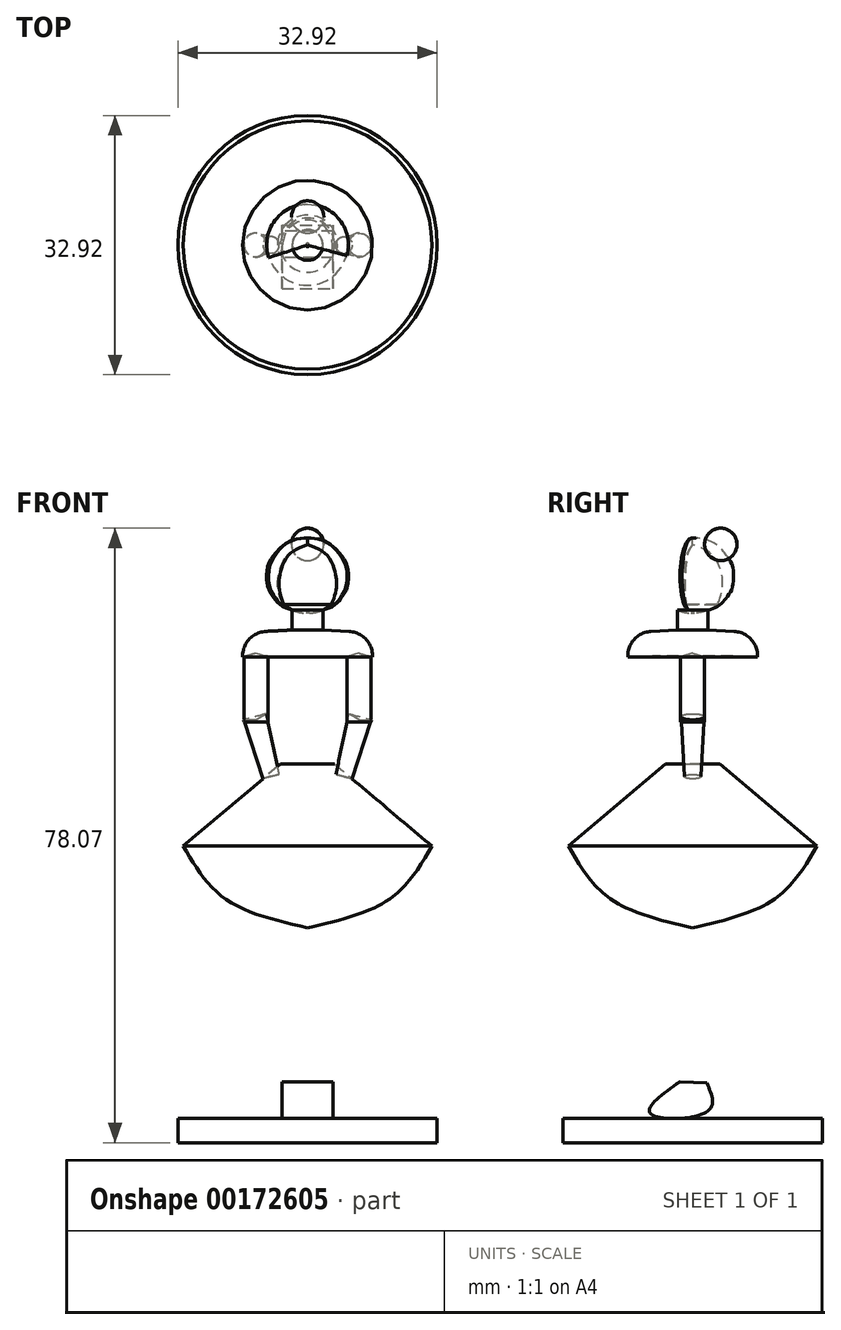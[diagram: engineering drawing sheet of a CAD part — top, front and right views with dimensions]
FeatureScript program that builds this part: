
annotation { "Feature Type Name" : "Feature", "Feature Type Description" : "" }
export const myFeature = defineFeature(function(context is Context, id is Id, definition is map)
    precondition{}
    {
        {
            var Q0;
            Q0=qCreatedBy(makeId("Front.planeOp"),FACE);
            var sketch = newSketch(context, id + "F0", { "sketchPlane" : qUnion([Q0])});
            skFitSpline(sketch, "E0", {"points": [v(-5.4, 24.75) * mm, v(-2.64, 17.55) * mm, v(-3.57, 10.2) * mm], "startDerivative": vector(6.92, -12.61) * mm, "endDerivative": vector(-2.97, -14.09) * mm});
            skLineSegment(sketch, "E1", {"start": v(0, 29.58) * mm, "end": v(0, 9.96) * mm});
            skFitSpline(sketch, "E2", {"points": [v(-3.57, 10.2) * mm, v(0, 9.96) * mm], "startDerivative": vector(3.3, 0.5) * mm, "endDerivative": vector(2.93, 1.66) * mm});
            skLineSegment(sketch, "E3", {"start": v(-5.4, 24.75) * mm, "end": v(0, 24.75) * mm});
            skPoint(sketch, "E3.endSnap0", {"position": v(0, 19.77) * mm});
            skSolve(sketch);
        }
        {
            var Q0;
            Q0 = qSketchRegion(id + "F0", true);
            var Q1;
            Q1=sQuery(id+"F0.wireOp",EDGE,"E0");
            var Q2;
            Q2=sQuery(id+"F0.wireOp",EDGE,"E2");
            var Q3;
            Q3=sQuery(id+"F0.wireOp",EDGE,"E1");
            revolve(context, id + "F1", {"bodyType" : ToolBodyType.SURFACE, "entities" : qUnion([Q0]), "surfaceEntities" : qUnion([Q1, Q2]), "axis" : qUnion([Q3]), "revolveType" : RevolveType.FULL});
        }
        {
            var Q0;
            Q0=qCreatedBy(makeId("Front.planeOp"),FACE);
            var sketch = newSketch(context, id + "F2", { "sketchPlane" : qUnion([Q0])});
            skArc(sketch, "E4", {"start": v(-5.27, 27.27) * mm, "mid": v(-7.42, 26.26) * mm, "end": v(-8.24, 24.04) * mm});
            skLineSegment(sketch, "E5", {"start": v(-8.24, 24.04) * mm, "end": v(-5.1, 24.14) * mm});
            skLineSegment(sketch, "E6", {"start": v(-5.27, 27.27) * mm, "end": v(0, 27.55) * mm});
            skLineSegment(sketch, "E7", {"start": v(-5.1, 24.14) * mm, "end": v(0, 24.14) * mm});
            skLineSegment(sketch, "E8", {"start": v(0, 24.14) * mm, "end": v(0, 27.55) * mm});
            skSolve(sketch);
        }
        {
            var Q0;
            Q0=makeQuery(id+"F2.imprint","IMPRINT",FACE,{"disambiguationData":[TD([[makeQuery(id+"F2.imprint","IMPRINT",EDGE,{"derivedFrom":sQuery(id+"F2.wireOp",EDGE,"E4")}),1.0]])]});
            var Q1;
            Q1=sQuery(id+"F2.wireOp",EDGE,"E8");
            revolve(context, id + "F3", {"entities" : qUnion([Q0]), "axis" : qUnion([Q1]), "revolveType" : RevolveType.FULL});
        }
        {
            var Q0;
            Q0=qCreatedBy(makeId("Front.planeOp"),FACE);
            var sketch = newSketch(context, id + "F4", { "sketchPlane" : qUnion([Q0])});
            skLineSegment(sketch, "E9", {"start": v(-8.05, 24.06) * mm, "end": v(-8.05, 15.74) * mm});
            skLineSegment(sketch, "E10", {"start": v(-8.05, 15.74) * mm, "end": v(-6.53, 15.74) * mm});
            skLineSegment(sketch, "E11", {"start": v(-6.53, 15.74) * mm, "end": v(-6.53, 24.5) * mm});
            skLineSegment(sketch, "E12", {"start": v(-6.53, 24.5) * mm, "end": v(-8.05, 24.06) * mm});
            skSolve(sketch);
        }
        {
            var Q0;
            Q0 = qSketchRegion(id + "F4", true);
            var Q1;
            Q1=sQuery(id+"F4.wireOp",EDGE,"E11");
            revolve(context, id + "F5", {"entities" : qUnion([Q0]), "axis" : qUnion([Q1]), "revolveType" : RevolveType.FULL});
        }
        {
            var Q0;
            Q0=qCreatedBy(makeId("Front.planeOp"),FACE);
            var sketch = newSketch(context, id + "F6", { "sketchPlane" : qUnion([Q0])});
            skLineSegment(sketch, "E13", {"start": v(-8.11, 16.04) * mm, "end": v(-5.66, 8.54) * mm});
            skLineSegment(sketch, "E14", {"start": v(-5.66, 8.54) * mm, "end": v(-4.64, 8.87) * mm});
            skLineSegment(sketch, "E15", {"start": v(-6.57, 16.04) * mm, "end": v(-4.64, 8.87) * mm});
            skLineSegment(sketch, "E16", {"start": v(-8.11, 16.04) * mm, "end": v(-6.57, 16.04) * mm});
            skSolve(sketch);
        }
        {
            var Q0;
            Q0 = qSketchRegion(id + "F6", true);
            var Q1;
            Q1=sQuery(id+"F6.wireOp",EDGE,"E15");
            revolve(context, id + "F7", {"entities" : qUnion([Q0]), "axis" : qUnion([Q1]), "revolveType" : RevolveType.FULL});
        }
        {
            var Q0;
            Q0=makeQuery(id+"F5.opRevolve","SWEPT_BODY",BODY,{"disambiguationData":[OSD([sQuery(id+"F4.wireOp",EDGE,"E9"),sQuery(id+"F4.wireOp",EDGE,"E10"),sQuery(id+"F4.wireOp",EDGE,"E11"),sQuery(id+"F4.wireOp",EDGE,"E12")])]});
            var Q1;
            Q1=qCreatedBy(makeId("Right.planeOp"),FACE);
            mirror(context, id + "F8", {"entities" : qUnion([Q0]), "mirrorPlane" : qUnion([Q1])});
        }
        {
            var Q0;
            Q0=makeQuery(id+"F7.opRevolve","SWEPT_BODY",BODY,{"disambiguationData":[OSD([sQuery(id+"F6.wireOp",EDGE,"E13"),sQuery(id+"F6.wireOp",EDGE,"E14"),sQuery(id+"F6.wireOp",EDGE,"E15"),sQuery(id+"F6.wireOp",EDGE,"E16")])]});
            var Q1;
            Q1=qCreatedBy(makeId("Right.planeOp"),FACE);
            mirror(context, id + "F9", {"entities" : qUnion([Q0]), "mirrorPlane" : qUnion([Q1])});
        }
        {
            var Q0;
            Q0=qCreatedBy(makeId("Front.planeOp"),FACE);
            var sketch = newSketch(context, id + "F10", { "sketchPlane" : qUnion([Q0])});
            skLineSegment(sketch, "E17", {"start": v(-1.94, 30.02) * mm, "end": v(-1.94, 27.15) * mm});
            skLineSegment(sketch, "E18", {"start": v(0, 30.02) * mm, "end": v(0, 27.15) * mm});
            skLineSegment(sketch, "E19", {"start": v(0, 27.15) * mm, "end": v(-1.94, 27.15) * mm});
            skLineSegment(sketch, "E20", {"start": v(0, 30.02) * mm, "end": v(-1.94, 30.02) * mm});
            skSolve(sketch);
        }
        {
            var Q0;
            Q0 = qSketchRegion(id + "F10", true);
            var Q1;
            Q1=sQuery(id+"F10.wireOp",EDGE,"E18");
            revolve(context, id + "F11", {"operationType" : NewBodyOperationType.ADD, "entities" : qUnion([Q0]), "axis" : qUnion([Q1]), "revolveType" : RevolveType.FULL});
        }
        {
            var Q0;
            Q0=qCreatedBy(makeId("Front.planeOp"),FACE);
            var sketch = newSketch(context, id + "F12", { "sketchPlane" : qUnion([Q0])});
            skArc(sketch, "E21", {"start": v(0, 38.84) * mm, "mid": v(-4.73, 34.22) * mm, "end": v(0, 29.6) * mm});
            skLineSegment(sketch, "E22", {"start": v(0, 38.84) * mm, "end": v(0, 29.6) * mm});
            skSolve(sketch);
        }
        {
            var Q0;
            Q0=makeQuery(id+"F12.imprint","IMPRINT",FACE,{"disambiguationData":[TD([[makeQuery(id+"F12.imprint","IMPRINT",EDGE,{"derivedFrom":sQuery(id+"F12.wireOp",EDGE,"E21")}),1.0]])]});
            var Q1;
            Q1=sQuery(id+"F12.wireOp",EDGE,"E22");
            revolve(context, id + "F13", {"operationType" : NewBodyOperationType.ADD, "entities" : qUnion([Q0]), "axis" : qUnion([Q1]), "revolveType" : RevolveType.FULL});
        }
        {
            var Q0;
            Q0=qCreatedBy(makeId("Right.planeOp"),FACE);
            var sketch = newSketch(context, id + "F14", { "sketchPlane" : qUnion([Q0])});
            skLineSegment(sketch, "E23", {"start": v(-4.55, 35.38) * mm, "end": v(-4.55, 34.16) * mm});
            skFitSpline(sketch, "E24", {"points": [v(-4.55, 35.38) * mm, v(-5.13, 34.53) * mm, v(-4.55, 34.16) * mm], "startDerivative": vector(-2.72, -1.48) * mm, "endDerivative": vector(2.77, -0.96) * mm});
            skSolve(sketch);
        }
        {
            var Q0;
            Q0 = qSketchRegion(id + "F14", true);
            var Q1;
            Q1=sQuery(id+"F14.wireOp",EDGE,"E23");
            revolve(context, id + "F15", {"operationType" : NewBodyOperationType.ADD, "entities" : qUnion([Q0]), "axis" : qUnion([Q1]), "revolveType" : RevolveType.FULL});
        }
        {
            var Q0;
            Q0=qCreatedBy(makeId("Front.planeOp"),FACE);
            var sketch = newSketch(context, id + "F16", { "sketchPlane" : qUnion([Q0])});
            skLineSegment(sketch, "E25", {"start": v(-3.45, 10.4) * mm, "end": v(-15.79, 0) * mm});
            skFitSpline(sketch, "E26", {"points": [v(-15.79, 0) * mm, v(-10.52, -6.65) * mm, v(0, -10.37) * mm], "startDerivative": vector(9.34, -16) * mm, "endDerivative": vector(21.94, -5) * mm});
            skLineSegment(sketch, "E27", {"start": v(0, 10.4) * mm, "end": v(0, -10.37) * mm});
            skLineSegment(sketch, "E28", {"start": v(-3.45, 10.4) * mm, "end": v(0, 10.4) * mm});
            skSolve(sketch);
        }
        {
            var Q0;
            Q0=makeQuery(id+"F16.imprint","IMPRINT",FACE,{"disambiguationData":[TD([[makeQuery(id+"F16.imprint","IMPRINT",EDGE,{"derivedFrom":sQuery(id+"F16.wireOp",EDGE,"E25")}),1.0]])]});
            var Q1;
            Q1=sQuery(id+"F16.wireOp",EDGE,"E27");
            revolve(context, id + "F17", {"entities" : qUnion([Q0]), "axis" : qUnion([Q1]), "revolveType" : RevolveType.FULL});
        }
        {
            var Q0;
            Q0=qCreatedBy(makeId("Top.planeOp"),FACE);
            var sketch = newSketch(context, id + "F18", { "sketchPlane" : qUnion([Q0])});
            skCircle(sketch, "E29", {"center": v(-1.68, 0) * mm, "radius": 1.68 * mm});
            skCircle(sketch, "E30", {"center": v(1.68, 0) * mm, "radius": 1.68 * mm});
            skSolve(sketch);
        }
        {
            var Q0;
            Q0=sQuery(id+"F18.wireOp",EDGE,"E29");
            var Q1;
            Q1=sQuery(id+"F18.wireOp",EDGE,"E30");
            extrude(context, id + "F19", {"bodyType" : ToolBodyType.SURFACE, "surfaceEntities" : qUnion([Q0, Q1]), "oppositeDirection" : true, "depth" : 30 * mm});
        }
        {
            var Q0;
            Q0=qCreatedBy(makeId("Right.planeOp"),FACE);
            var sketch = newSketch(context, id + "F20", { "sketchPlane" : qUnion([Q0])});
            skFitSpline(sketch, "E31", {"points": [v(1.78, -30.09) * mm, v(1.95, -33.66) * mm, v(-5.35, -33.98) * mm, v(-1.62, -29.93) * mm], "startDerivative": vector(6.7, -15.08) * mm, "endDerivative": vector(19.98, 14.31) * mm});
            skLineSegment(sketch, "E32", {"start": v(-1.62, -29.93) * mm, "end": v(1.78, -30.09) * mm});
            skSolve(sketch);
        }
        {
            var Q0;
            Q0 = qSketchRegion(id + "F20", true);
            var Q1;
            Q1=sQuery(id+"F20.wireOp",EDGE,"E31");
            extrude(context, id + "F21", {"entities" : qUnion([Q0]), "surfaceEntities" : qUnion([Q1]), "depth" : 3.25 * mm, "hasSecondDirection" : true, "secondDirectionOppositeDirection" : true, "secondDirectionDepth" : 3.25 * mm});
        }
        {
            var Q0;
            Q0=qCreatedBy(makeId("Front.planeOp"),FACE);
            var sketch = newSketch(context, id + "F22", { "sketchPlane" : qUnion([Q0])});
            skFitSpline(sketch, "E33", {"points": [v(0, 38.3) * mm, v(-2.5, 36.99) * mm, v(-3.58, 34.94) * mm, v(-3.8, 33.62) * mm, v(-3.7, 32.32) * mm, v(-3.16, 30.71) * mm], "startDerivative": vector(-11.37, -4.07) * mm, "endDerivative": vector(3.4, -8.54) * mm});
            skFitSpline(sketch, "E34", {"points": [v(-3.16, 30.71) * mm, v(-2.58, 30.3) * mm, v(-1.97, 29.99) * mm], "startDerivative": vector(1.13, -0.84) * mm, "endDerivative": vector(1.25, -0.6) * mm});
            skLineSegment(sketch, "E35", {"start": v(0, 38.3) * mm, "end": v(0, 39.11) * mm});
            skFitSpline(sketch, "E36", {"points": [v(0, 39.11) * mm, v(-0.78, 39.11) * mm, v(-2.47, 38.61) * mm, v(-3.85, 37.49) * mm, v(-4.92, 35.9) * mm, v(-5.19, 34.57) * mm, v(-5, 32.7) * mm, v(-4.24, 31.47) * mm, v(-3.77, 30.9) * mm, v(-2.97, 30.32) * mm, v(-1.97, 29.99) * mm], "startDerivative": vector(-9.09, 0.69) * mm, "endDerivative": vector(11.5, -3) * mm});
            skLineSegment(sketch, "E37", {"start": v(0, 39.11) * mm, "end": v(0, 29.98) * mm});
            skPoint(sketch, "E37.endSnap0", {"position": v(0, 38.7) * mm});
            skSolve(sketch);
        }
        {
            var Q0;
            Q0 = qSketchRegion(id + "F22", true);
            var Q1;
            Q1=sQuery(id+"F22.wireOp",EDGE,"E37");
            revolve(context, id + "F23", {"entities" : qUnion([Q0]), "axis" : qUnion([Q1]), "revolveType" : RevolveType.TWO_DIRECTIONS, "angle" : 195 * degree, "angleBack" : 342.05 * degree});
        }
        {
            var Q0;
            Q0=qCreatedBy(makeId("Right.planeOp"),FACE);
            var sketch = newSketch(context, id + "F24", { "sketchPlane" : qUnion([Q0])});
            skFitSpline(sketch, "E38", {"points": [v(0, 39.14) * mm, v(-1.3, 39.05) * mm, v(-3.03, 38.41) * mm, v(-3.92, 37.62) * mm, v(-4.13, 36.84) * mm, v(-2.99, 35.89) * mm, v(-1.96, 34.3) * mm, v(-1.53, 32.72) * mm, v(-1.35, 31.68) * mm, v(-1.21, 30.58) * mm, v(-0.92, 30) * mm], "startDerivative": vector(-12.02, 0.57) * mm, "endDerivative": vector(4.67, -7.2) * mm});
            skLineSegment(sketch, "E39", {"start": v(-0.92, 30) * mm, "end": v(-0.53, 30) * mm});
            skLineSegment(sketch, "E40", {"start": v(0, 39.14) * mm, "end": v(0, 30.01) * mm});
            skSolve(sketch);
        }
        {
            var Q0;
            Q0 = qSketchRegion(id + "F24", true);
            var Q1;
            Q1=sQuery(id+"F24.wireOp",EDGE,"E38");
            var Q2;
            Q2=sQuery(id+"F24.wireOp",EDGE,"E40");
            revolve(context, id + "F25", {"bodyType" : ToolBodyType.SURFACE, "entities" : qUnion([Q0]), "surfaceEntities" : qUnion([Q1]), "axis" : qUnion([Q2]), "revolveType" : RevolveType.FULL});
        }
        {
            var Q0;
            Q0=qCreatedBy(makeId("Right.planeOp"),FACE);
            var sketch = newSketch(context, id + "F26", { "sketchPlane" : qUnion([Q0])});
            skArc(sketch, "E41", {"start": v(3.24, 36.3) * mm, "mid": v(5.21, 39.57) * mm, "end": v(1.53, 38.55) * mm});
            skLineSegment(sketch, "E42", {"start": v(0.85, 40.55) * mm, "end": v(6.2, 36.17) * mm});
            skSolve(sketch);
        }
        {
            var Q0;
            Q0 = qSketchRegion(id + "F26", true);
            var Q1;
            Q1=sQuery(id+"F26.wireOp",EDGE,"E42");
            revolve(context, id + "F27", {"entities" : qUnion([Q0]), "axis" : qUnion([Q1]), "revolveType" : RevolveType.FULL});
        }
        {
            var Q0;
            Q0=qCreatedBy(makeId("Front.planeOp"),FACE);
            var sketch = newSketch(context, id + "F28", { "sketchPlane" : qUnion([Q0])});
            skLineSegment(sketch, "E43", {"start": v(0, -34.6) * mm, "end": v(0, -37.68) * mm});
            skLineSegment(sketch, "E44", {"start": v(0, -37.68) * mm, "end": v(-16.46, -37.68) * mm});
            skLineSegment(sketch, "E45", {"start": v(0, -34.6) * mm, "end": v(-16.46, -34.6) * mm});
            skLineSegment(sketch, "E46", {"start": v(-16.46, -34.6) * mm, "end": v(-16.46, -37.68) * mm});
            skSolve(sketch);
        }
        {
            var Q0;
            Q0=makeQuery(id+"F28.imprint","IMPRINT",FACE,{"disambiguationData":[TD([[makeQuery(id+"F28.imprint","IMPRINT",EDGE,{"derivedFrom":sQuery(id+"F28.wireOp",EDGE,"E43")}),-1.0]])]});
            var Q1;
            Q1=sQuery(id+"F28.wireOp",EDGE,"E43");
            revolve(context, id + "F29", {"entities" : qUnion([Q0]), "axis" : qUnion([Q1]), "revolveType" : RevolveType.FULL});
        }
    });
